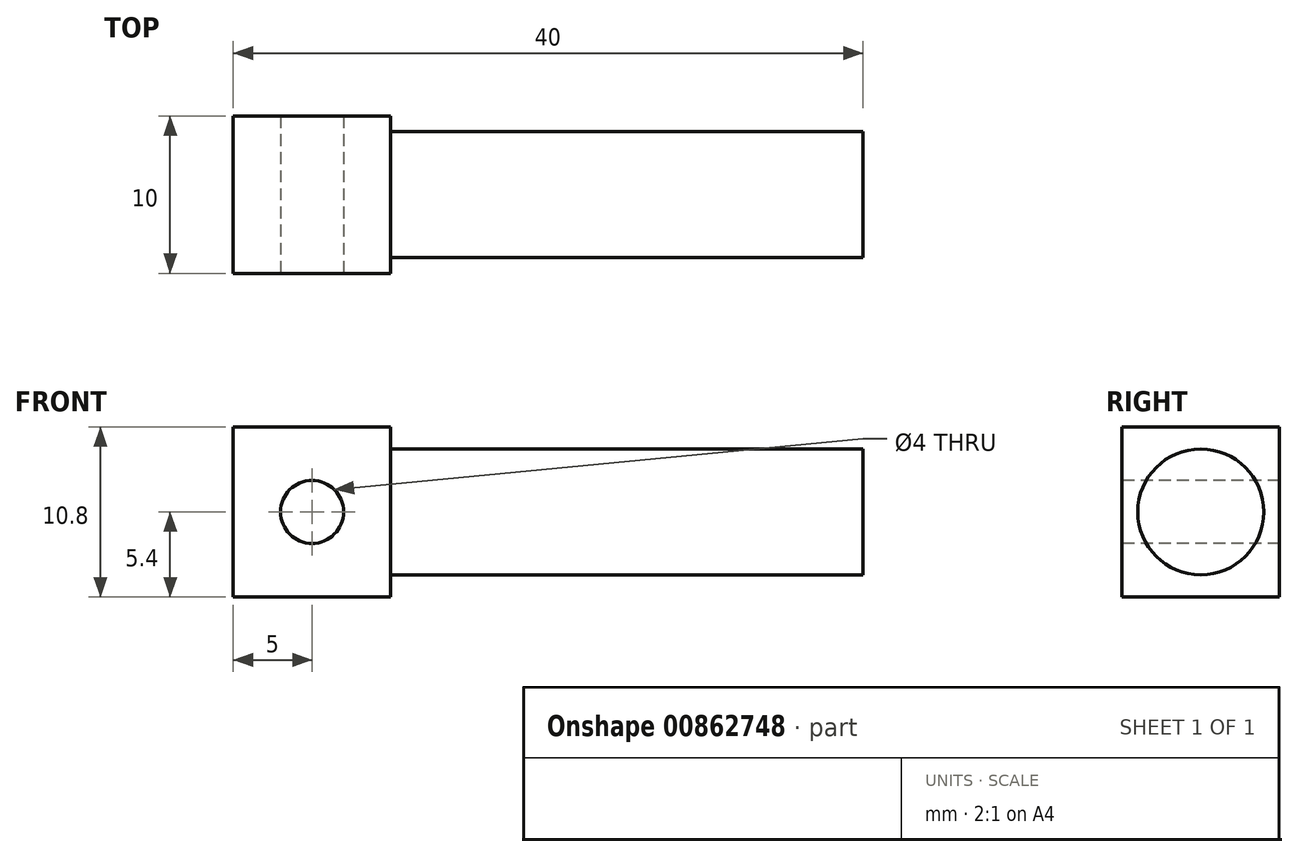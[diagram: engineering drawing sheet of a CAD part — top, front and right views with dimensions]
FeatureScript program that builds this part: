
annotation { "Feature Type Name" : "Feature", "Feature Type Description" : "" }
export const myFeature = defineFeature(function(context is Context, id is Id, definition is map)
    precondition{}
    {
        {
            var Q0;
            Q0=qCreatedBy(makeId("Right.planeOp"),FACE);
            var sketch = newSketch(context, id + "F0", { "sketchPlane" : qUnion([Q0])});
            skLineSegment(sketch, "E0.bottom", {"start": v(11.27, 0) * mm, "end": v(21.27, 0) * mm});
            skLineSegment(sketch, "E0.top", {"start": v(11.27, 10.8) * mm, "end": v(21.27, 10.8) * mm});
            skLineSegment(sketch, "E0.left", {"start": v(11.27, 0) * mm, "end": v(11.27, 10.8) * mm});
            skLineSegment(sketch, "E0.right", {"start": v(21.27, 0) * mm, "end": v(21.27, 10.8) * mm});
            skSolve(sketch);
        }
        {
            var Q0;
            Q0 = qSketchRegion(id + "F0", true);
            extrude(context, id + "F1", {"entities" : qUnion([Q0]), "depth" : 10 * mm, "offsetDistance" : 25 * mm});
        }
        {
            var Q0;
            Q0=makeQuery(id+"F1.opExtrude","CAP_FACE",FACE,{"disambiguationData":[OSD([sQuery(id+"F0.wireOp",EDGE,"E0.bottom"),sQuery(id+"F0.wireOp",EDGE,"E0.top"),sQuery(id+"F0.wireOp",EDGE,"E0.left"),sQuery(id+"F0.wireOp",EDGE,"E0.right")])],"isStart":false});
            var sketch = newSketch(context, id + "F2", { "sketchPlane" : qUnion([Q0])});
            skCircle(sketch, "E1", {"center": v(16.27, 5.4) * mm, "radius": 4 * mm});
            skSolve(sketch);
        }
        {
            var Q0;
            Q0 = qSketchRegion(id + "F2", true);
            extrude(context, id + "F3", {"entities" : qUnion([Q0]), "operationType" : NewBodyOperationType.ADD, "depth" : 30 * mm, "offsetDistance" : 25 * mm});
        }
        {
            var Q0;
            Q0=makeQuery(id+"F1.opExtrude","SWEPT_FACE",FACE,{"disambiguationData":[OSD([sQuery(id+"F0.wireOp",EDGE,"E0.left")])]});
            var sketch = newSketch(context, id + "F4", { "sketchPlane" : qUnion([Q0])});
            skCircle(sketch, "E2", {"center": v(5, 5.4) * mm, "radius": 2 * mm});
            skPoint(sketch, "E2.centerSnap0", {"position": v(10, 5.4) * mm});
            skPoint(sketch, "E2.centerSnap1", {"position": v(5, 10.8) * mm});
            skSolve(sketch);
        }
        {
            var Q0;
            Q0 = qSketchRegion(id + "F4", true);
            extrude(context, id + "F5", {"entities" : qUnion([Q0]), "operationType" : NewBodyOperationType.REMOVE, "oppositeDirection" : true, "depth" : 25 * mm, "offsetDistance" : 25 * mm});
        }
    });
